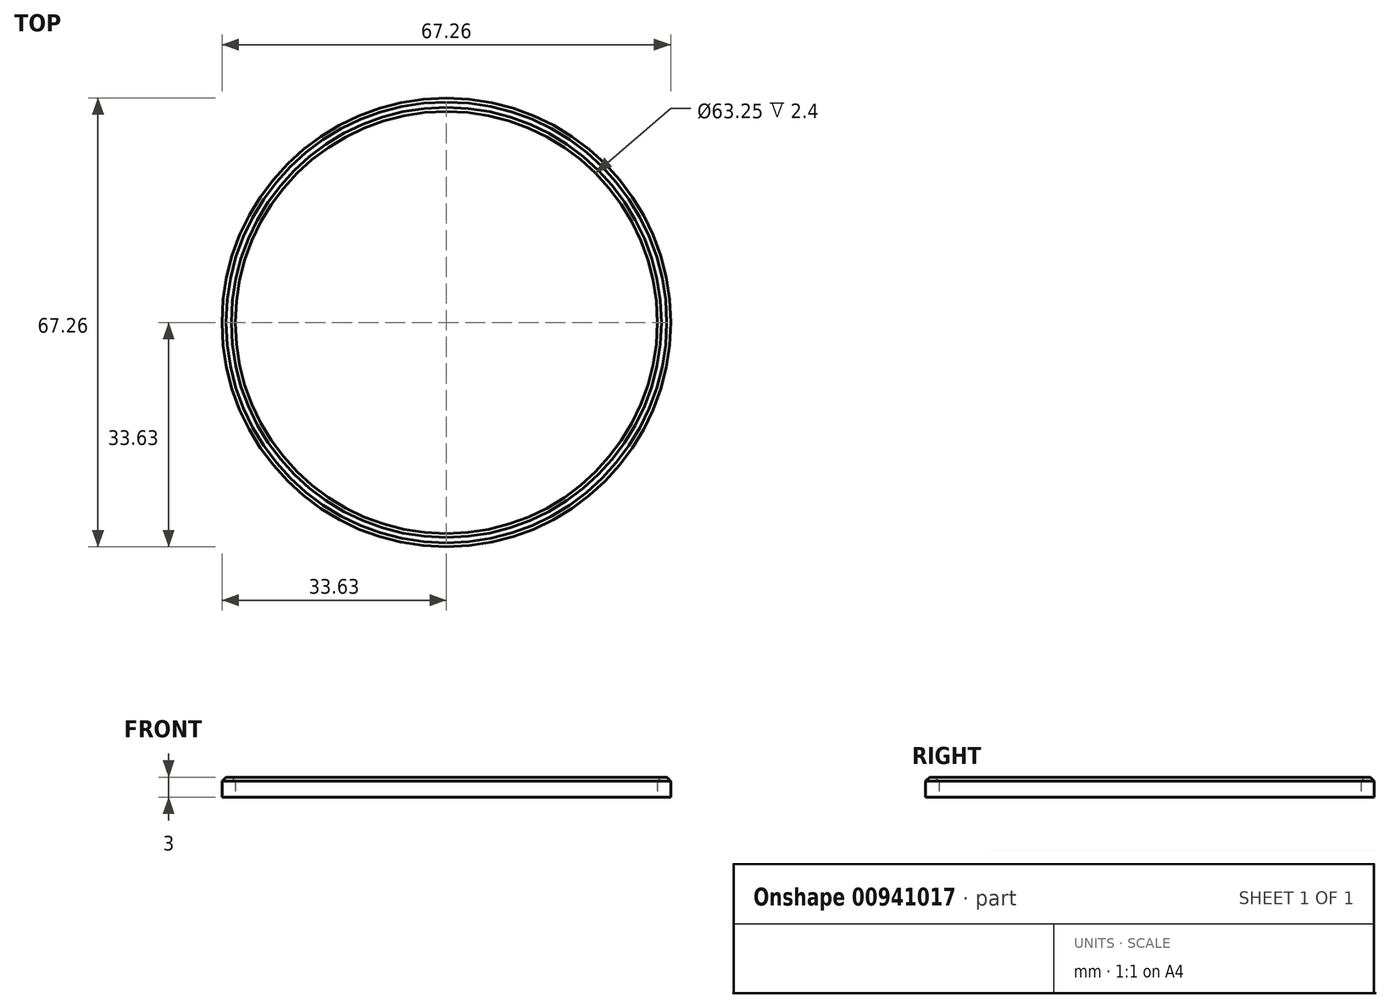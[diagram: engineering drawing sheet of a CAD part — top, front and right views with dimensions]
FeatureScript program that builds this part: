
annotation { "Feature Type Name" : "Feature", "Feature Type Description" : "" }
export const myFeature = defineFeature(function(context is Context, id is Id, definition is map)
    precondition{}
    {
        {
            var Q0;
            Q0=qCreatedBy(makeId("Top.planeOp"),FACE);
            var sketch = newSketch(context, id + "F0", { "sketchPlane" : qUnion([Q0])});
            skCircle(sketch, "E0", {"center": v(0, 0) * mm, "radius": 33.62 * mm});
            skCircle(sketch, "E1", {"center": v(0, 0) * mm, "radius": 31.62 * mm});
            skSolve(sketch);
        }
        {
            var Q0;
            Q0=makeQuery(id+"F0.imprint","IMPRINT",FACE,{"disambiguationData":[TD([[makeQuery(id+"F0.imprint","IMPRINT",EDGE,{"derivedFrom":sQuery(id+"F0.wireOp",EDGE,"E0")}),1.0]])]});
            extrude(context, id + "F1", {"entities" : qUnion([Q0]), "depth" : 3 * mm, "offsetDistance" : 25 * mm});
        }
        {
            var Q0;
            Q0=makeQuery(id+"F1.opExtrude","CAP_EDGE",EDGE,{"disambiguationData":[OSD([sQuery(id+"F0.wireOp",EDGE,"E0")])],"isStart":false});
            var Q1;
            Q1=makeQuery(id+"F1.opExtrude","CAP_EDGE",EDGE,{"disambiguationData":[OSD([sQuery(id+"F0.wireOp",EDGE,"E1")])],"isStart":false});
            chamfer(context, id + "F2", {"entities" : qUnion([Q0, Q1]), "width" : 0.6 * mm, "tangentPropagation" : true});
        }
    });
